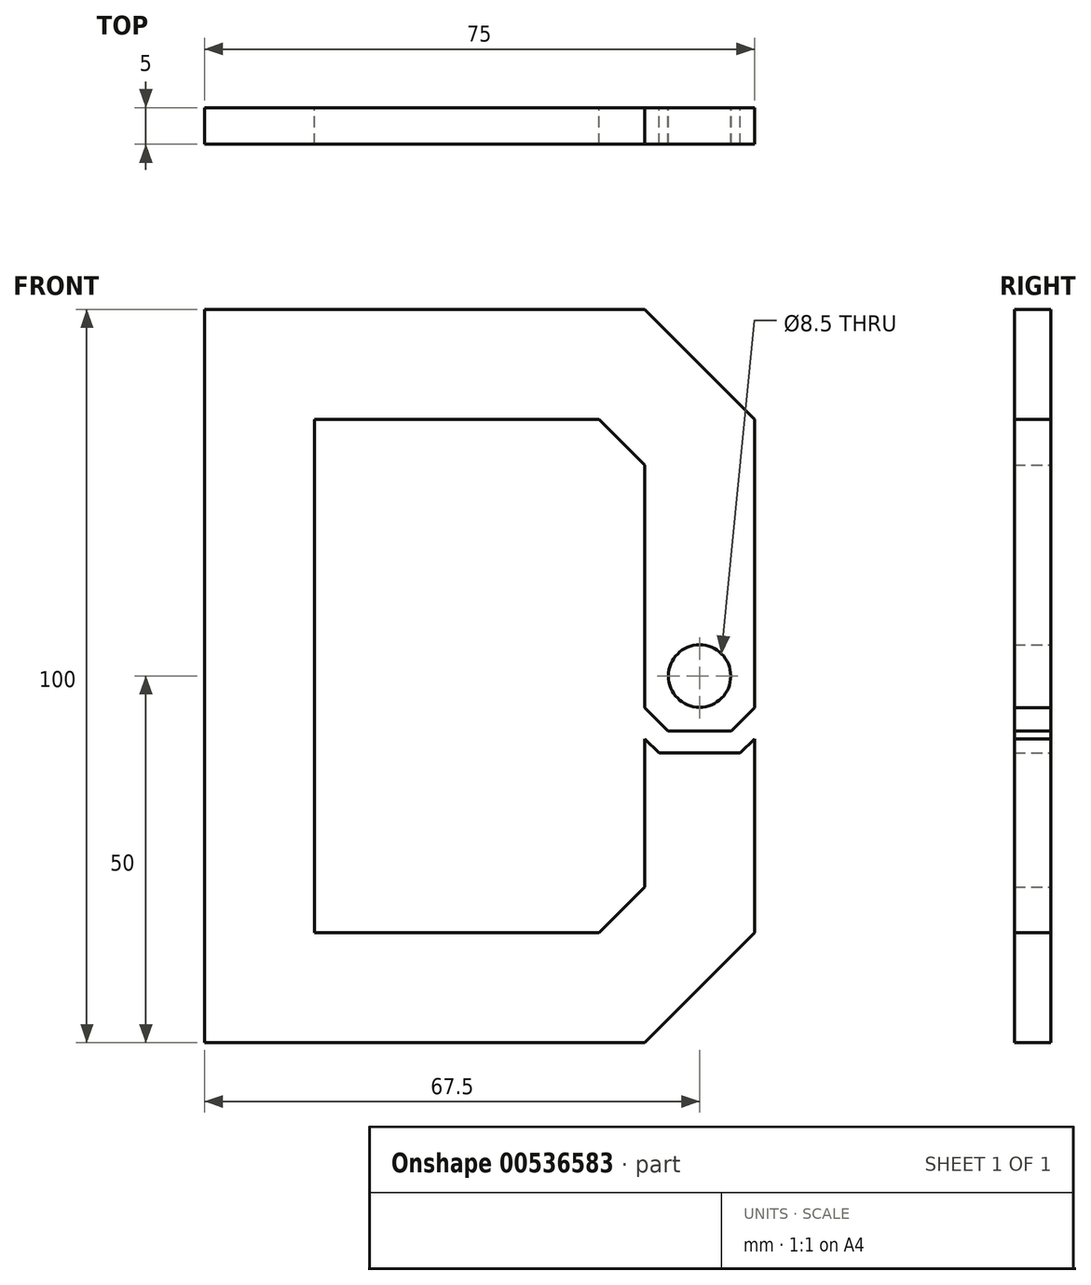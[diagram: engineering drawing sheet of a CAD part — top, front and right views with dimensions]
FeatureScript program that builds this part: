
annotation { "Feature Type Name" : "Feature", "Feature Type Description" : "" }
export const myFeature = defineFeature(function(context is Context, id is Id, definition is map)
    precondition{}
    {
        {
            var Q0;
            Q0=qCreatedBy(makeId("Front.planeOp"),FACE);
            var sketch = newSketch(context, id + "F0", { "sketchPlane" : qUnion([Q0])});
            skLineSegment(sketch, "E0", {"start": v(0, 0) * mm, "end": v(0, 100) * mm});
            skLineSegment(sketch, "E1", {"start": v(0, 100) * mm, "end": v(60, 100) * mm});
            skLineSegment(sketch, "E2", {"start": v(60, 100) * mm, "end": v(75, 85) * mm});
            skLineSegment(sketch, "E3", {"start": v(75, 85) * mm, "end": v(75, 45.7) * mm});
            skLineSegment(sketch, "E4", {"start": v(75, 15) * mm, "end": v(60, 0) * mm});
            skLineSegment(sketch, "E5", {"start": v(60, 0) * mm, "end": v(0, 0) * mm});
            skLineSegment(sketch, "E6", {"start": v(60, 50) * mm, "end": v(75, 50) * mm, "construction": true});
            skLineSegment(sketch, "E7.0", {"start": v(53.79, 15) * mm, "end": v(15, 15) * mm});
            skLineSegment(sketch, "E7.1", {"start": v(15, 85) * mm, "end": v(53.79, 85) * mm});
            skLineSegment(sketch, "E7.2", {"start": v(53.79, 85) * mm, "end": v(60, 78.79) * mm});
            skLineSegment(sketch, "E7.3", {"start": v(15, 15) * mm, "end": v(15, 85) * mm});
            skLineSegment(sketch, "E7.4", {"start": v(60, 78.79) * mm, "end": v(60, 45.7) * mm});
            skLineSegment(sketch, "E7.5", {"start": v(60, 21.21) * mm, "end": v(53.79, 15) * mm});
            skCircle(sketch, "E8", {"center": v(67.5, 50) * mm, "radius": 4.25 * mm});
            skLineSegment(sketch, "E9", {"start": v(60, 45.7) * mm, "end": v(63.2, 42.5) * mm});
            skLineSegment(sketch, "E10", {"start": v(63.2, 42.5) * mm, "end": v(71.8, 42.5) * mm});
            skLineSegment(sketch, "E11", {"start": v(71.8, 42.5) * mm, "end": v(75, 45.7) * mm});
            skLineSegment(sketch, "E12", {"start": v(67.5, 50) * mm, "end": v(67.5, 42.5) * mm, "construction": true});
            skLineSegment(sketch, "E13", {"start": v(61.6, 44.1) * mm, "end": v(64.5, 47) * mm, "construction": true});
            skLineSegment(sketch, "E14.0", {"start": v(73.04, 39.5) * mm, "end": v(75, 41.46) * mm});
            skLineSegment(sketch, "E14.1", {"start": v(61.96, 39.5) * mm, "end": v(73.04, 39.5) * mm});
            skLineSegment(sketch, "E14.2", {"start": v(60, 41.46) * mm, "end": v(61.96, 39.5) * mm});
            skLineSegment(sketch, "E15.trimOffspring", {"start": v(60, 41.46) * mm, "end": v(60, 21.21) * mm});
            skLineSegment(sketch, "E16.trimOffspring", {"start": v(75, 41.46) * mm, "end": v(75, 15) * mm});
            skLineSegment(sketch, "E17", {"start": v(75, 45.7) * mm, "end": v(71.8, 45.7) * mm, "construction": true});
            skLineSegment(sketch, "E18", {"start": v(71.8, 45.7) * mm, "end": v(71.8, 42.5) * mm, "construction": true});
            skSolve(sketch);
        }
        {
            var Q0;
            Q0=makeQuery(id+"F0.imprint","IMPRINT",FACE,{"disambiguationData":[TD([[makeQuery(id+"F0.imprint","IMPRINT",EDGE,{"derivedFrom":sQuery(id+"F0.wireOp",EDGE,"E0")}),-1.0]])]});
            extrude(context, id + "F1", {"entities" : qUnion([Q0]), "depth" : 5 * mm, "offsetDistance" : 25 * mm});
        }
    });
